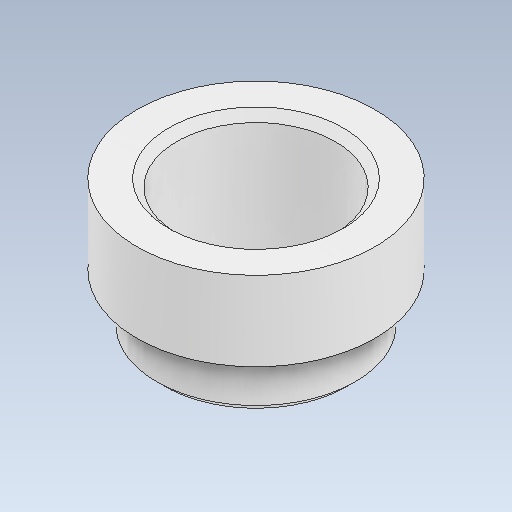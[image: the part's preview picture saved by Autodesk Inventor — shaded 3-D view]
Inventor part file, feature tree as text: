
AUTODESK INVENTOR PART (.ipt)
format: ipt  version: 2020 (Build 240168000, 168)  size: 133,632 bytes
history: native  units: mm
features: extrude x3, other x1, sketch x1, chamfer x1
ambient origin geometry x8: Origin, YZ Plane, XZ Plane, XY Plane, X Axis, Y Axis, Z Axis, Center Point
bodies: Body1 (feature_tree)
feature tree (6):
  other  "Bryła1"
  sketch  "Szkic1"
  extrude  "Wyciągnięcie proste1"  Depth=30.0mm
  extrude  "Wyciągnięcie proste2"  Depth=20.0mm
  extrude  "Wyciągnięcie proste3"  Depth=25.0mm
  chamfer  "Faza1"  Distance=17.0mm
